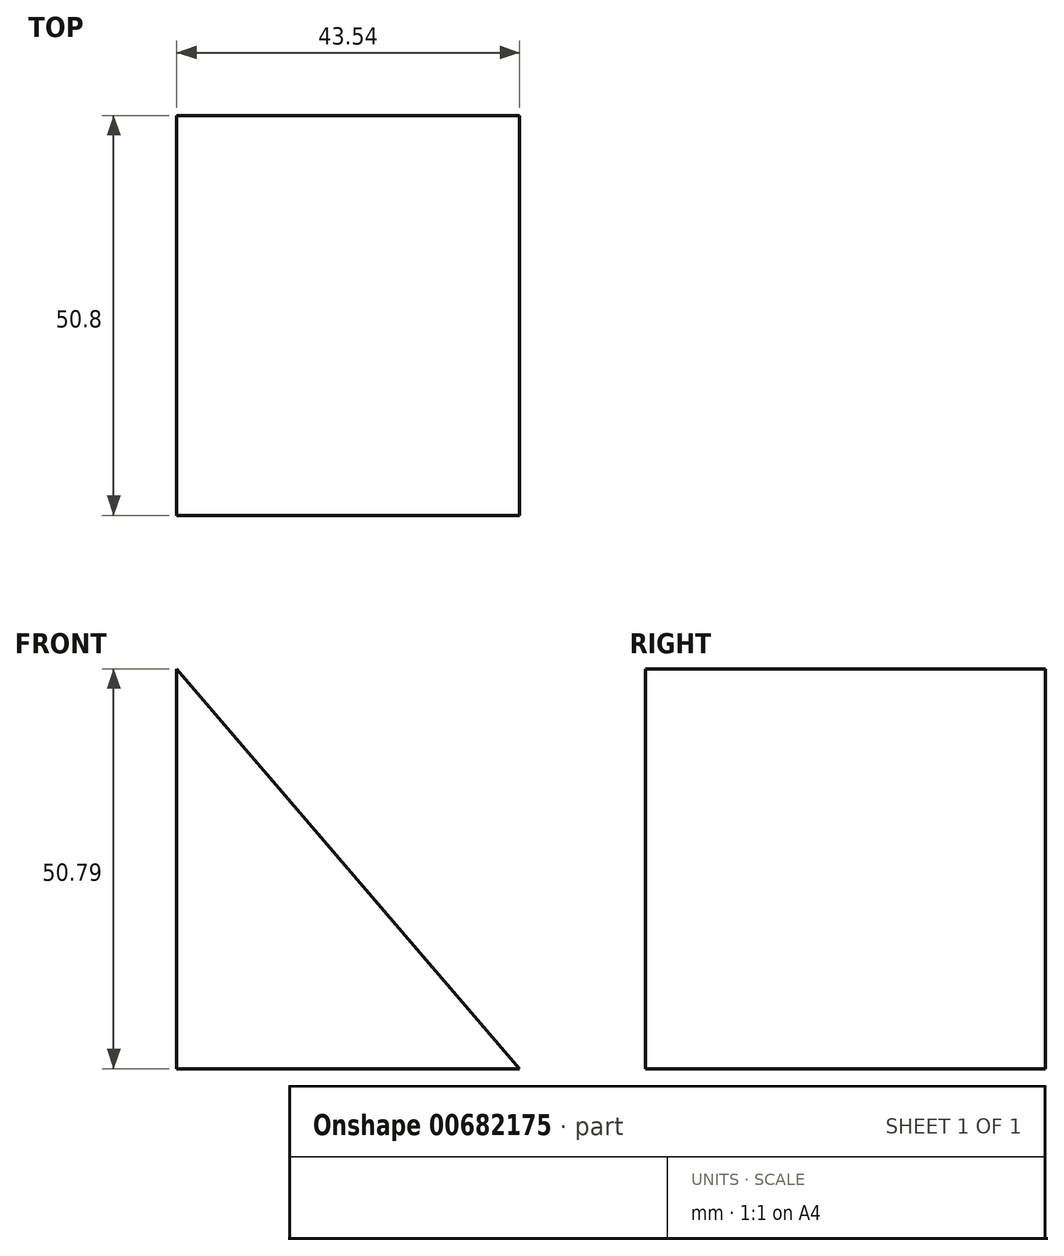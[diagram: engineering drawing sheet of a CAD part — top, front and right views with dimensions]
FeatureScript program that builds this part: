
annotation { "Feature Type Name" : "Feature", "Feature Type Description" : "" }
export const myFeature = defineFeature(function(context is Context, id is Id, definition is map)
    precondition{}
    {
        {
            var Q0;
            Q0=qCreatedBy(makeId("Front.planeOp"),FACE);
            var sketch = newSketch(context, id + "F0", { "sketchPlane" : qUnion([Q0])});
            skLineSegment(sketch, "E0", {"start": v(-64.83, 53.94) * mm, "end": v(-64.83, 3.15) * mm});
            skLineSegment(sketch, "E1", {"start": v(-64.83, 3.15) * mm, "end": v(-21.3, 3.15) * mm});
            skLineSegment(sketch, "E2", {"start": v(-64.83, 53.94) * mm, "end": v(-21.3, 3.15) * mm});
            skSolve(sketch);
        }
        {
            var Q0;
            Q0 = qSketchRegion(id + "F0", true);
            extrude(context, id + "F1", {"entities" : qUnion([Q0]), "depth" : 50.8 * mm, "offsetDistance" : 25.4 * mm});
        }
    });
